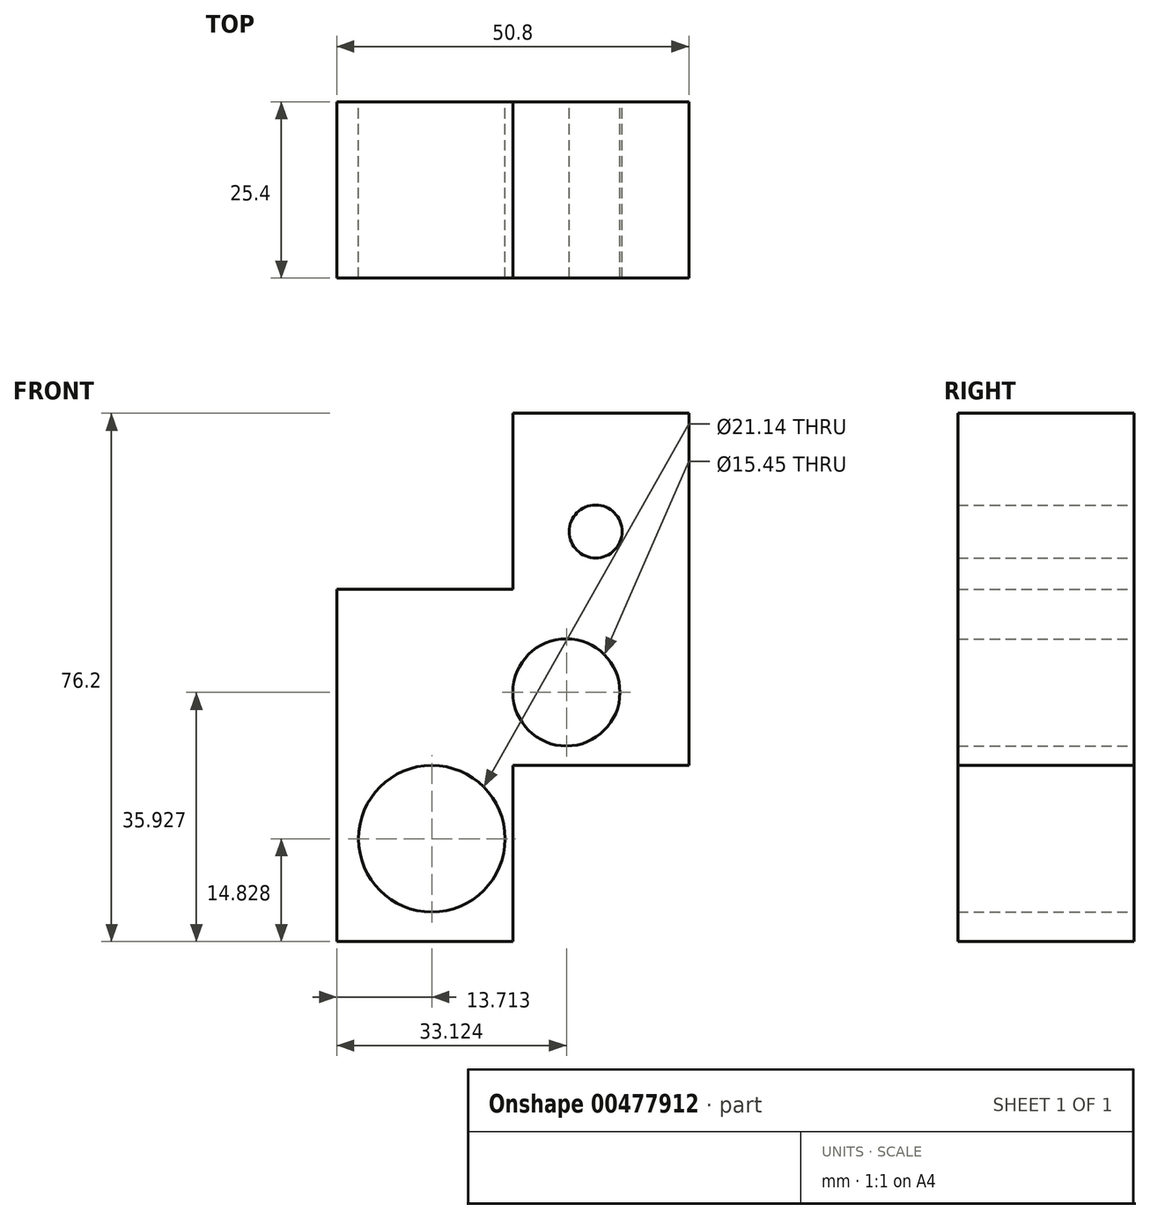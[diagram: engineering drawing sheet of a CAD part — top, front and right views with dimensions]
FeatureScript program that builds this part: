
annotation { "Feature Type Name" : "Feature", "Feature Type Description" : "" }
export const myFeature = defineFeature(function(context is Context, id is Id, definition is map)
    precondition{}
    {
        {
            var Q0;
            Q0=qCreatedBy(makeId("Front.planeOp"),FACE);
            var sketch = newSketch(context, id + "F0", { "sketchPlane" : qUnion([Q0])});
            skLineSegment(sketch, "E0.top", {"start": v(0, -25.4) * mm, "end": v(25.4, -25.4) * mm});
            skLineSegment(sketch, "E0.left", {"start": v(0, 0) * mm, "end": v(0, -25.4) * mm});
            skLineSegment(sketch, "E0.right", {"start": v(25.4, 0) * mm, "end": v(25.4, -25.4) * mm});
            skLineSegment(sketch, "E1.left", {"start": v(0, 0) * mm, "end": v(0, 25.4) * mm});
            skLineSegment(sketch, "E1.right", {"start": v(50.8, 0) * mm, "end": v(50.8, 25.4) * mm});
            skLineSegment(sketch, "E2.bottom", {"start": v(50.8, 0) * mm, "end": v(25.4, 0) * mm});
            skLineSegment(sketch, "E2.top", {"start": v(50.8, 50.8) * mm, "end": v(25.4, 50.8) * mm});
            skLineSegment(sketch, "E2.left", {"start": v(50.8, 0) * mm, "end": v(50.8, 50.8) * mm});
            skLineSegment(sketch, "E3", {"start": v(0, 25.4) * mm, "end": v(25.4, 25.4) * mm});
            skLineSegment(sketch, "E4", {"start": v(25.4, 25.4) * mm, "end": v(25.4, 50.8) * mm});
            skCircle(sketch, "E5", {"center": v(33.12, 10.53) * mm, "radius": 7.72 * mm});
            skCircle(sketch, "E6", {"center": v(13.71, -10.57) * mm, "radius": 10.57 * mm});
            skCircle(sketch, "E7", {"center": v(37.34, 33.73) * mm, "radius": 3.82 * mm});
            skSolve(sketch);
        }
        {
            var Q0;
            Q0=makeQuery(id+"F0.imprint","IMPRINT",FACE,{"disambiguationData":[TD([[makeQuery(id+"F0.imprint","IMPRINT",EDGE,{"derivedFrom":sQuery(id+"F0.wireOp",EDGE,"E0.top")}),1.0]])]});
            extrude(context, id + "F1", {"entities" : qUnion([Q0]), "depth" : 25.4 * mm});
        }
    });
